# Revit family: Doors-Sliding_WON-DOOR_Fireguard-MFW-Straight_
name_source: partatom
category: Doors
units: mm (PartAtom-declared; Revit-internal decimal feet)

## family parameters
Always vertical = Yes
Cut with Voids When Loaded = No
Host = Wall
OmniClass Number = 23.17.11.31
Room Calculation Point = No
Shared = No

## types (2) — shared parameters
Description = The Won-Door FireGuard MFW (Movable fire wall) product is U.L. Certified as meeting the criteria required by ANSI/UL263 (ASTM E119). When the building code restricts the size of openings in a Fire Barrier, the FireGuard MFW provides a viable solution. The FireGuard MFW is available in the following U.L. ratings: MFWI (1-hour) or MFWII (2-hour).
Door Finish = Won-Door-Metal-Platinum
Lookup Table = Doors-Sliding_WON-DOOR_Fireguard-MFW-Straight
Manufacturer = Won-Door Corporation
Model = Fireguard MFW Straight
Offset for Backing Depth = 0' - 6 1/8"
Offset for Backing Width = 0' - 3 1/8"
Product Page URL = https://www.wondoor.com
Product data url = https://www.bimobject.com
Thickness = 1' - 8"
URL = https://www.wondoor.com
Version = 1
Wall Closure = By host

## per-type parameters (varying)
| type | Fire Rating | Offset for Stack Depth | Pocket Thickness |
| 60 Minute | 60 Minute Fire Rating | 0' - 4 7/8" | 2' - 5 3/4" |
| 120 Minute | 120 Minute Fire Rating | 0' - 6 1/8" | 2' - 8 1/4" |

## geometry (parser evidence)
native form markers: Sweep x4
no freeform markers — native parametric forms only
